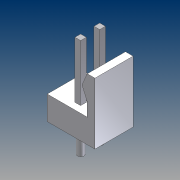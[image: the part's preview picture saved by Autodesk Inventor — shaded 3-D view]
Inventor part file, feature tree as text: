
AUTODESK INVENTOR PART (.ipt)
format: ipt  version: unknown  size: 198,656 bytes
history: native  units: mm (DEFAULTED — no unit token found)
features: extrude x3, plane x3, sketch x2, pattern_linear x1
ambient origin geometry x5: Origin, X Axis, Y Axis, Z Axis, Center Point
feature tree (9):
  extrude  "Extrusion1"  Depth=3.175mm
  sketch  "Sketch3"  dims[d2=8.1788mm d3=1.4478mm d4=1.016mm d5=2.54mm d6=0.0mm d7=0.762mm d8=2.794mm d9=0.0mm d10=10.668mm d11=0.0mm d12=20.0mm d14=2.54mm d15=0.889mm]
  extrude  "Extrusion2"  Depth=1.4478mm
  extrude  "Extrusion3"  Depth=1.016mm
  pattern_linear  "Rectangular Pattern1"  Spacing1=2.54mm  [1 undecoded]
  plane  "YZ Plane (RIGHT)"
  plane  "XZ Plane (TOP)"
  plane  "XY Plane (FRONT)"
  sketch  "Sketch2"  dims[d0=6.35mm d1=3.175mm]
note: 1 required parameter value undecoded (feature->parameter linkage not recoverable at this tier; creation-order binding heuristic only, values carry confidence <= 0.55)
